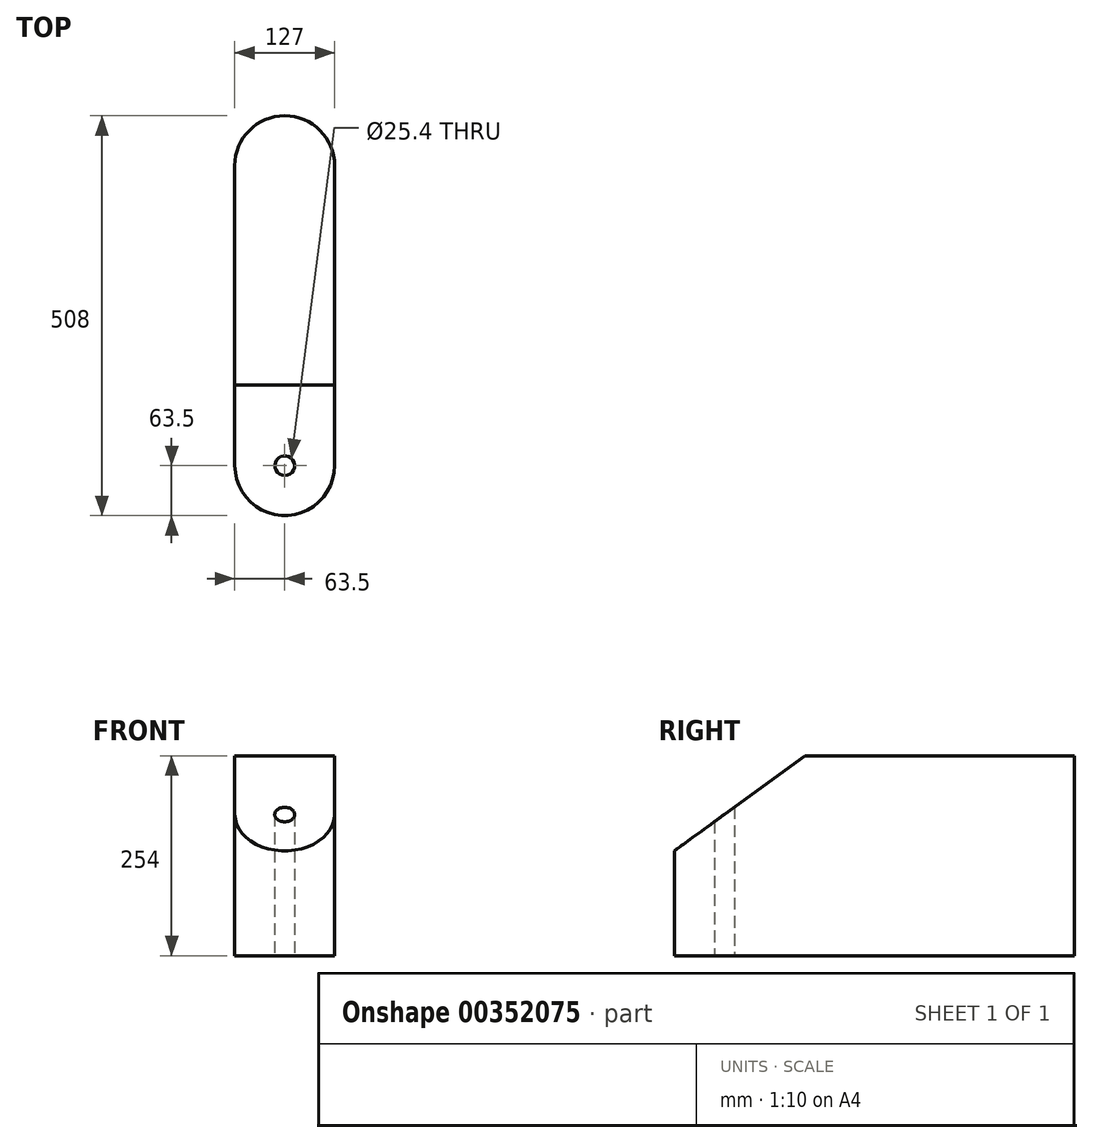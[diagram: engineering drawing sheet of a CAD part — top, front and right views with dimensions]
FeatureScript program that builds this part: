
annotation { "Feature Type Name" : "Feature", "Feature Type Description" : "" }
export const myFeature = defineFeature(function(context is Context, id is Id, definition is map)
    precondition{}
    {
        {
            var Q0;
            Q0=qCreatedBy(makeId("Top.planeOp"),FACE);
            var sketch = newSketch(context, id + "F0", { "sketchPlane" : qUnion([Q0])});
            skCircle(sketch, "E0", {"center": v(0, 0) * mm, "radius": 63.5 * mm});
            skLineSegment(sketch, "E1.bottom", {"start": v(-63.5, 0) * mm, "end": v(63.5, 0) * mm});
            skLineSegment(sketch, "E1.top", {"start": v(-63.5, -381) * mm, "end": v(63.5, -381) * mm});
            skLineSegment(sketch, "E1.left", {"start": v(-63.5, 0) * mm, "end": v(-63.5, -381) * mm});
            skLineSegment(sketch, "E1.right", {"start": v(63.5, 0) * mm, "end": v(63.5, -381) * mm});
            skCircle(sketch, "E2", {"center": v(0, -381) * mm, "radius": 63.5 * mm});
            skSolve(sketch);
        }
        {
            var Q0;
            Q0=qSketchRegion(id+"F0",true);
            extrude(context, id + "F1", {"entities" : qUnion([Q0]), "depth" : 254 * mm});
        }
        {
            var Q0;
            Q0=qCreatedBy(makeId("Right.planeOp"),FACE);
            var sketch = newSketch(context, id + "F2", { "sketchPlane" : qUnion([Q0])});
            skLineSegment(sketch, "E3", {"start": v(-487.07, 102) * mm, "end": v(-204.59, 308.1) * mm});
            skLineSegment(sketch, "E4", {"start": v(-204.59, 308.1) * mm, "end": v(-487.07, 308.1) * mm});
            skLineSegment(sketch, "E5", {"start": v(-487.07, 308.1) * mm, "end": v(-487.07, 102) * mm});
            skSolve(sketch);
        }
        {
            var Q0;
            Q0 = qSketchRegion(id + "F2", true);
            extrude(context, id + "F3", {"entities" : qUnion([Q0]), "operationType" : NewBodyOperationType.REMOVE, "oppositeDirection" : true, "depth" : 254 * mm, "hasSecondDirection" : true, "secondDirectionOppositeDirection" : false, "secondDirectionDepth" : 254 * mm});
        }
        {
            var Q0;
            Q0=qCreatedBy(makeId("Top.planeOp"),FACE);
            var sketch = newSketch(context, id + "F4", { "sketchPlane" : qUnion([Q0])});
            skCircle(sketch, "E6", {"center": v(0, -381) * mm, "radius": 12.7 * mm});
            skSolve(sketch);
        }
        {
            var Q0;
            Q0 = qSketchRegion(id + "F4", true);
            extrude(context, id + "F5", {"entities" : qUnion([Q0]), "operationType" : NewBodyOperationType.REMOVE, "depth" : 254 * mm});
        }
    });
